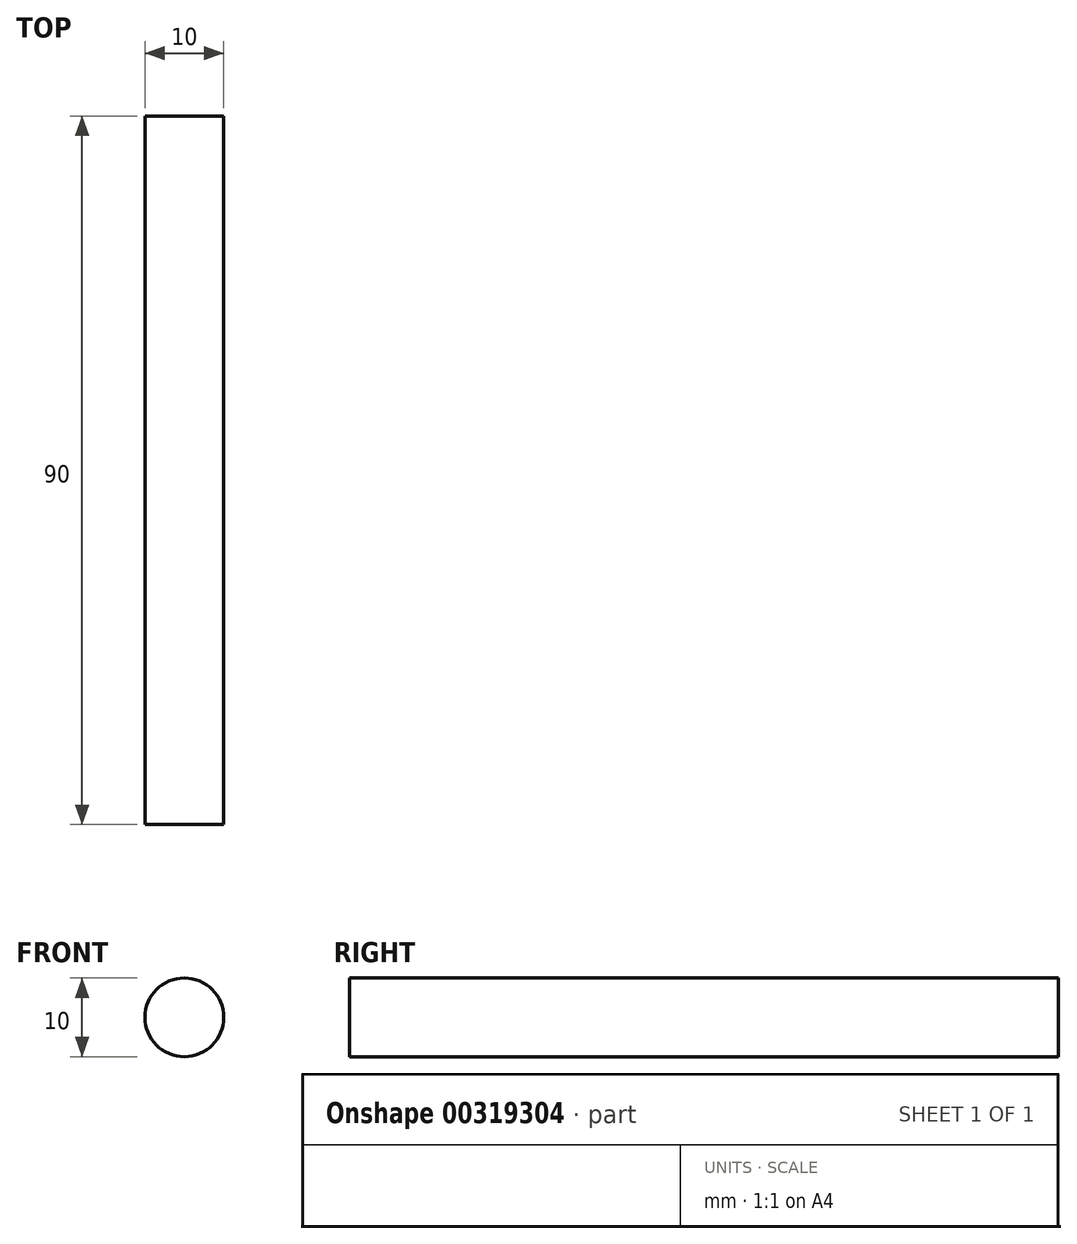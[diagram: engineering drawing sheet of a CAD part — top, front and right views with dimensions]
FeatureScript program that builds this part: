
annotation { "Feature Type Name" : "Feature", "Feature Type Description" : "" }
export const myFeature = defineFeature(function(context is Context, id is Id, definition is map)
    precondition{}
    {
        {
            var Q0;
            Q0=qCreatedBy(makeId("Front.planeOp"),FACE);
            var sketch = newSketch(context, id + "F0", { "sketchPlane" : qUnion([Q0])});
            skCircle(sketch, "E0", {"center": v(0, 0) * mm, "radius": 5 * mm});
            skSolve(sketch);
        }
        {
            var Q0;
            Q0 = qSketchRegion(id + "F0", true);
            extrude(context, id + "F1", {"entities" : qUnion([Q0]), "depth" : 90 * mm});
        }
    });
